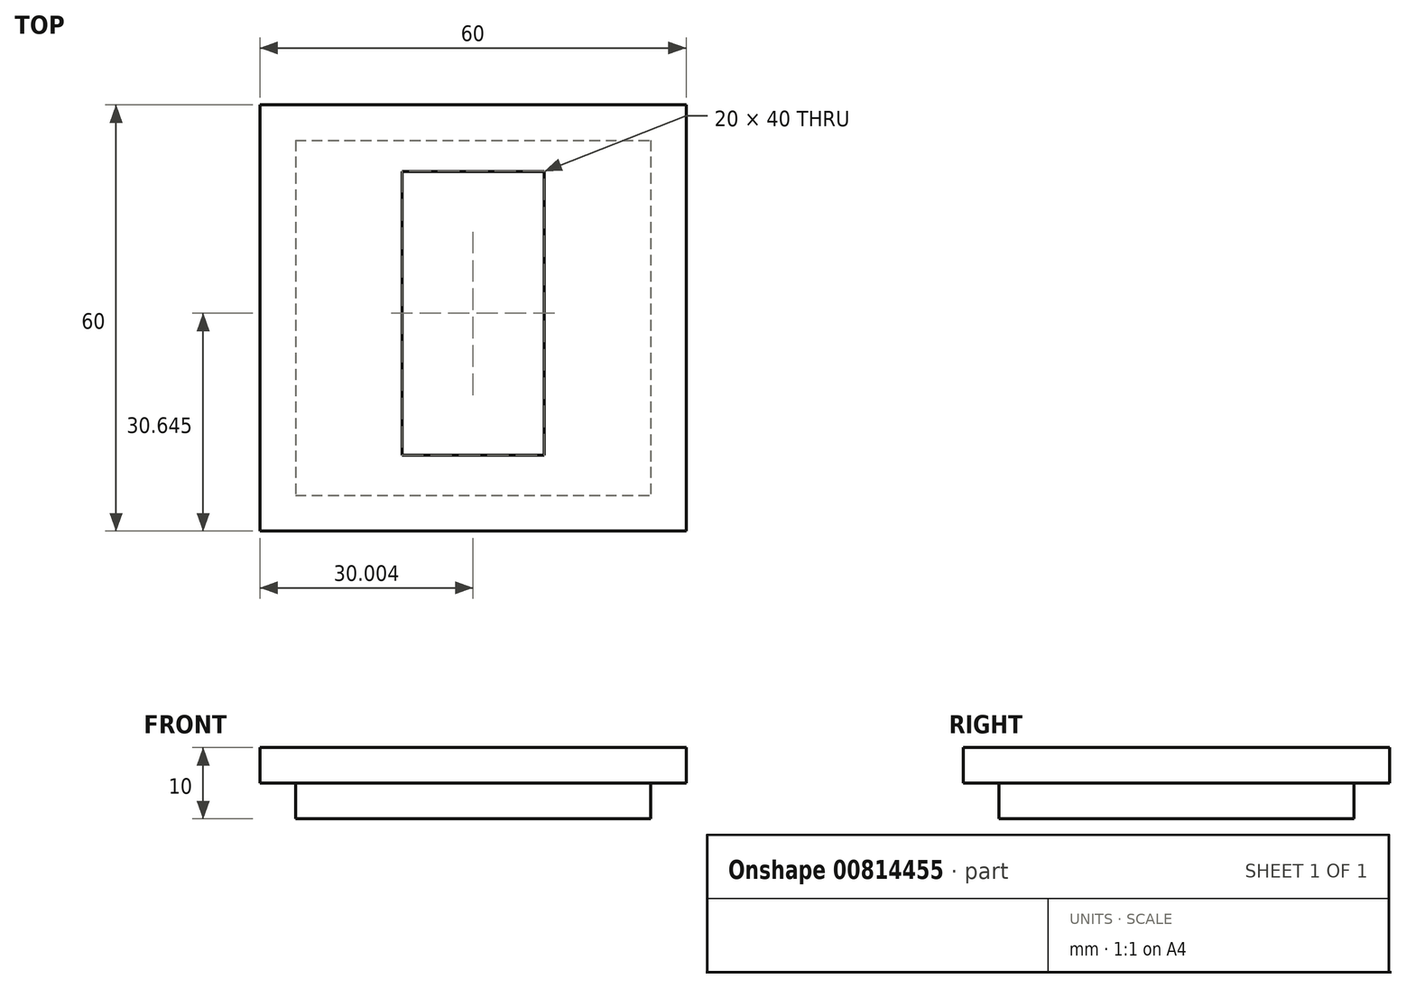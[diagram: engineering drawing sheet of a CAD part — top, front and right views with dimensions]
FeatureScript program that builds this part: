
annotation { "Feature Type Name" : "Feature", "Feature Type Description" : "" }
export const myFeature = defineFeature(function(context is Context, id is Id, definition is map)
    precondition{}
    {
        {
            var Q0;
            Q0=qCreatedBy(makeId("Top.planeOp"),FACE);
            var sketch = newSketch(context, id + "F0", { "sketchPlane" : qUnion([Q0])});
            skLineSegment(sketch, "E0.bottom", {"start": v(-51.17, -24.51) * mm, "end": v(8.83, -24.51) * mm});
            skLineSegment(sketch, "E0.top", {"start": v(-51.17, 35.49) * mm, "end": v(8.83, 35.49) * mm});
            skLineSegment(sketch, "E0.left", {"start": v(-51.17, -24.51) * mm, "end": v(-51.17, 35.49) * mm});
            skLineSegment(sketch, "E0.right", {"start": v(8.83, -24.51) * mm, "end": v(8.83, 35.49) * mm});
            skSolve(sketch);
        }
        {
            var Q0;
            Q0=makeQuery(id+"F0.imprint","IMPRINT",FACE,{"disambiguationData":[TD([[makeQuery(id+"F0.imprint","IMPRINT",EDGE,{"derivedFrom":sQuery(id+"F0.wireOp",EDGE,"E0.bottom")}),1.0]])]});
            extrude(context, id + "F1", {"entities" : qUnion([Q0]), "depth" : 5 * mm, "offsetDistance" : 25.4 * mm});
        }
        {
            var Q0;
            Q0=makeQuery(id+"F1.opExtrude","CAP_FACE",FACE,{"disambiguationData":[OSD([sQuery(id+"F0.wireOp",EDGE,"E0.bottom"),sQuery(id+"F0.wireOp",EDGE,"E0.top"),sQuery(id+"F0.wireOp",EDGE,"E0.left"),sQuery(id+"F0.wireOp",EDGE,"E0.right")])],"isStart":true});
            var sketch = newSketch(context, id + "F2", { "sketchPlane" : qUnion([Q0])});
            skLineSegment(sketch, "E1.bottom", {"start": v(-46.17, -30.49) * mm, "end": v(3.83, -30.49) * mm});
            skLineSegment(sketch, "E1.top", {"start": v(-46.17, 19.51) * mm, "end": v(3.83, 19.51) * mm});
            skLineSegment(sketch, "E1.left", {"start": v(-46.17, -30.49) * mm, "end": v(-46.17, 19.51) * mm});
            skLineSegment(sketch, "E1.right", {"start": v(3.83, -30.49) * mm, "end": v(3.83, 19.51) * mm});
            skSolve(sketch);
        }
        {
            var Q0;
            Q0=makeQuery(id+"F2.imprint","IMPRINT",FACE,{"disambiguationData":[TD([[makeQuery(id+"F2.imprint","IMPRINT",EDGE,{"derivedFrom":sQuery(id+"F2.wireOp",EDGE,"E1.bottom")}),1.0]])]});
            extrude(context, id + "F3", {"entities" : qUnion([Q0]), "operationType" : NewBodyOperationType.ADD, "depth" : 5 * mm, "offsetDistance" : 25.4 * mm});
        }
        {
            var Q0;
            Q0=makeQuery(id+"F1.opExtrude","CAP_FACE",FACE,{"disambiguationData":[OSD([sQuery(id+"F0.wireOp",EDGE,"E0.bottom"),sQuery(id+"F0.wireOp",EDGE,"E0.top"),sQuery(id+"F0.wireOp",EDGE,"E0.left"),sQuery(id+"F0.wireOp",EDGE,"E0.right")])],"isStart":false});
            var sketch = newSketch(context, id + "F4", { "sketchPlane" : qUnion([Q0])});
            skLineSegment(sketch, "E2.bottom", {"start": v(-31.17, 26.14) * mm, "end": v(-11.17, 26.14) * mm});
            skLineSegment(sketch, "E2.top", {"start": v(-31.17, -13.86) * mm, "end": v(-11.17, -13.86) * mm});
            skLineSegment(sketch, "E2.left", {"start": v(-31.17, 26.14) * mm, "end": v(-31.17, -13.86) * mm});
            skLineSegment(sketch, "E2.right", {"start": v(-11.17, 26.14) * mm, "end": v(-11.17, -13.86) * mm});
            skSolve(sketch);
        }
        {
            var Q0;
            Q0 = qSketchRegion(id + "F4", true);
            extrude(context, id + "F5", {"entities" : qUnion([Q0]), "operationType" : NewBodyOperationType.REMOVE, "oppositeDirection" : true, "depth" : 10 * mm, "offsetDistance" : 25.4 * mm});
        }
    });
